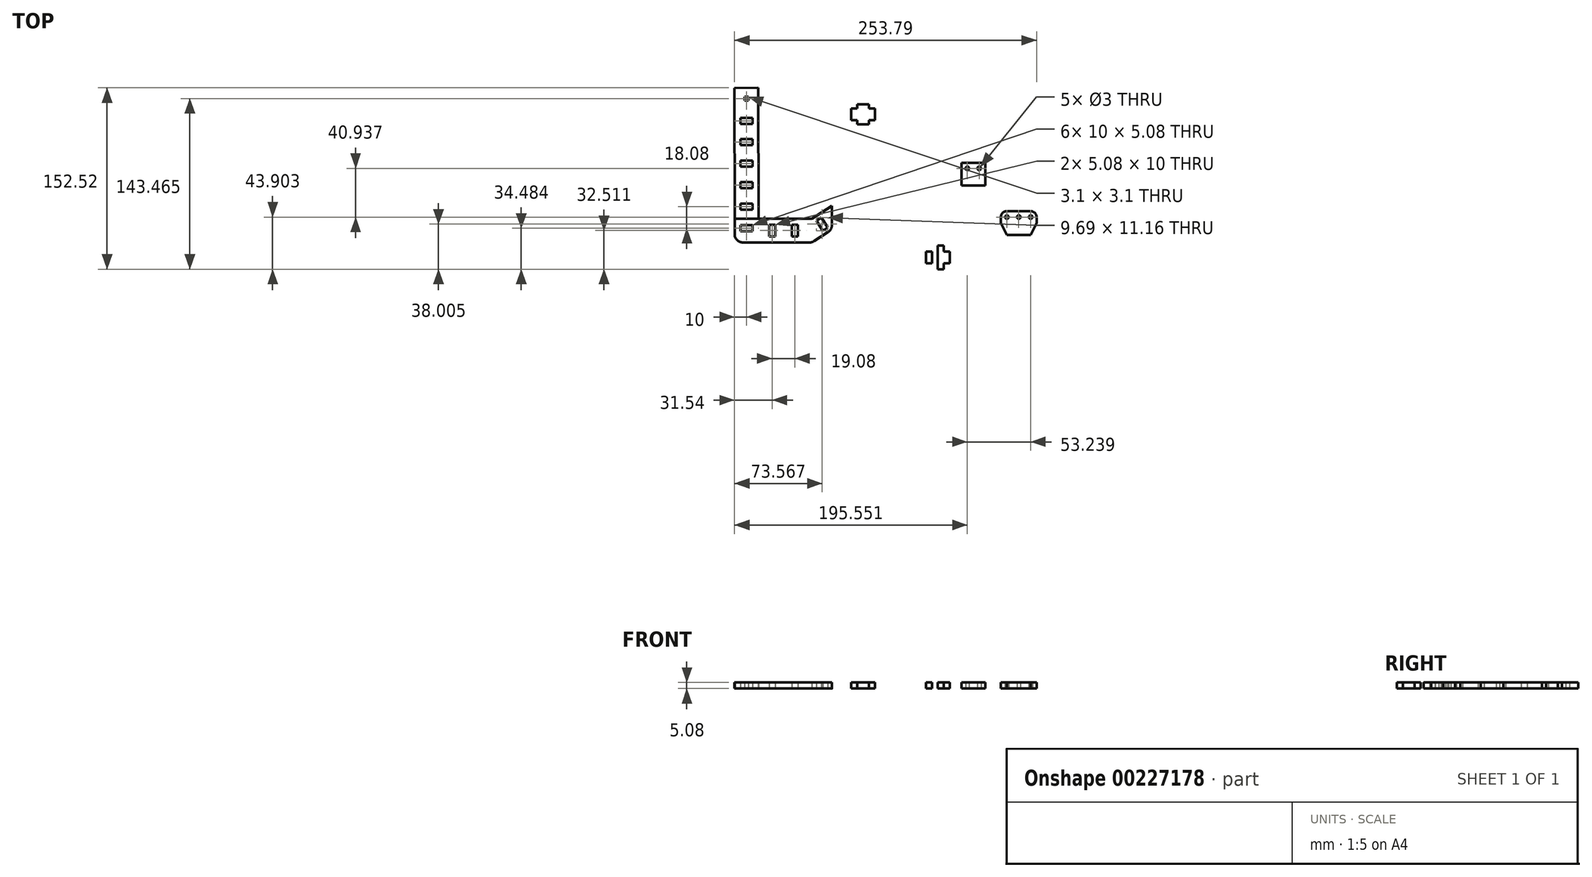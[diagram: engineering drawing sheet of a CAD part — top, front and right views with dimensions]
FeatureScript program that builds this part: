
annotation { "Feature Type Name" : "Feature", "Feature Type Description" : "" }
export const myFeature = defineFeature(function(context is Context, id is Id, definition is map)
    precondition{}
    {
        {
            var Q0;
            Q0=qCreatedBy(makeId("Top.planeOp"),FACE);
            var sketch = newSketch(context, id + "F0", { "sketchPlane" : qUnion([Q0])});
            skLineSegment(sketch, "E0.bottom", {"start": v(-72.75, 135.47) * mm, "end": v(-52.75, 135.48) * mm});
            skLineSegment(sketch, "E0.left", {"start": v(-72.75, 135.47) * mm, "end": v(-72.71, 25.47) * mm});
            skLineSegment(sketch, "E1.bottom", {"start": v(-57.75, 92.3) * mm, "end": v(-67.75, 92.3) * mm});
            skLineSegment(sketch, "E1.top", {"start": v(-57.75, 87.22) * mm, "end": v(-67.75, 87.22) * mm});
            skLineSegment(sketch, "E1.left", {"start": v(-57.75, 92.3) * mm, "end": v(-57.75, 87.22) * mm});
            skLineSegment(sketch, "E1.right", {"start": v(-67.75, 92.3) * mm, "end": v(-67.75, 87.22) * mm});
            skPoint(sketch, "E1.middle", {"position": v(-62.75, 89.76) * mm});
            skPoint(sketch, "E1.middle.positionSnap0", {"position": v(-62.75, 135.47) * mm});
            skLineSegment(sketch, "E2", {"start": v(-52.75, 135.48) * mm, "end": v(-52.71, 25.48) * mm});
            skLineSegment(sketch, "E3.bottom", {"start": v(-67.75, 74.22) * mm, "end": v(-57.75, 74.22) * mm});
            skLineSegment(sketch, "E3.top", {"start": v(-67.75, 69.14) * mm, "end": v(-57.75, 69.14) * mm});
            skLineSegment(sketch, "E3.left", {"start": v(-67.75, 74.22) * mm, "end": v(-67.75, 69.14) * mm});
            skLineSegment(sketch, "E3.right", {"start": v(-57.75, 74.22) * mm, "end": v(-57.75, 69.14) * mm});
            skLineSegment(sketch, "E4.bottom", {"start": v(117.8, 72.3) * mm, "end": v(137.8, 72.3) * mm});
            skLineSegment(sketch, "E4.top", {"start": v(117.8, 63.3) * mm, "end": v(137.8, 63.3) * mm});
            skLineSegment(sketch, "E4.left", {"start": v(117.8, 72.3) * mm, "end": v(117.8, 63.3) * mm});
            skLineSegment(sketch, "E4.right", {"start": v(137.8, 72.3) * mm, "end": v(137.8, 63.3) * mm});
            skCircle(sketch, "E5", {"center": v(122.8, 67.8) * mm, "radius": 1.5 * mm});
            skPoint(sketch, "E5.centerSnap0", {"position": v(117.8, 67.8) * mm});
            skLineSegment(sketch, "E6", {"start": v(127.8, 63.3) * mm, "end": v(127.8, 72.3) * mm, "construction": true});
            skCircle(sketch, "E7.MirrorC", {"center": v(132.8, 67.8) * mm, "radius": 1.5 * mm});
            skLineSegment(sketch, "E8.top", {"start": v(117.8, 53.3) * mm, "end": v(137.8, 53.3) * mm});
            skLineSegment(sketch, "E8.left", {"start": v(117.8, 63.3) * mm, "end": v(117.8, 53.3) * mm});
            skLineSegment(sketch, "E8.right", {"start": v(137.8, 63.3) * mm, "end": v(137.8, 53.3) * mm});
            skLineSegment(sketch, "E9.bottom", {"start": v(-57.75, 110.38) * mm, "end": v(-67.75, 110.38) * mm});
            skLineSegment(sketch, "E9.top", {"start": v(-57.75, 105.3) * mm, "end": v(-67.75, 105.3) * mm});
            skLineSegment(sketch, "E9.left", {"start": v(-57.75, 110.38) * mm, "end": v(-57.75, 105.3) * mm});
            skLineSegment(sketch, "E9.right", {"start": v(-67.75, 110.38) * mm, "end": v(-67.75, 105.3) * mm});
            skLineSegment(sketch, "E10", {"start": v(-67.75, 71.68) * mm, "end": v(-57.75, 71.68) * mm});
            skLineSegment(sketch, "E11.MirrorCS", {"start": v(-67.75, 51.06) * mm, "end": v(-67.75, 56.14) * mm});
            skLineSegment(sketch, "E12.MirrorCS", {"start": v(-57.75, 56.14) * mm, "end": v(-67.75, 56.14) * mm});
            skLineSegment(sketch, "E13.MirrorCS", {"start": v(-57.75, 51.06) * mm, "end": v(-57.75, 56.14) * mm});
            skLineSegment(sketch, "E14.MirrorCS", {"start": v(-57.75, 51.06) * mm, "end": v(-67.75, 51.06) * mm});
            skLineSegment(sketch, "E15", {"start": v(-67.75, 53.6) * mm, "end": v(-57.75, 53.6) * mm});
            skLineSegment(sketch, "E16.bottom", {"start": v(93.14, 2.96) * mm, "end": v(102.98, 2.96) * mm});
            skLineSegment(sketch, "E16.top", {"start": v(93.14, -17.04) * mm, "end": v(102.98, -17.04) * mm});
            skLineSegment(sketch, "E16.left", {"start": v(93.14, 2.96) * mm, "end": v(93.14, -17.04) * mm});
            skLineSegment(sketch, "E16.right", {"start": v(102.98, 2.96) * mm, "end": v(102.98, -17.04) * mm});
            skLineSegment(sketch, "E17.bottom", {"start": v(93.14, -2.04) * mm, "end": v(88.06, -2.04) * mm});
            skLineSegment(sketch, "E17.top", {"start": v(93.14, -12.04) * mm, "end": v(88.06, -12.04) * mm});
            skLineSegment(sketch, "E17.left", {"start": v(93.14, -2.04) * mm, "end": v(93.14, -12.04) * mm});
            skLineSegment(sketch, "E17.right", {"start": v(88.06, -2.04) * mm, "end": v(88.06, -12.04) * mm});
            skLineSegment(sketch, "E18", {"start": v(98.06, 2.96) * mm, "end": v(98.06, -17.04) * mm});
            skLineSegment(sketch, "E19.MirrorCS", {"start": v(102.98, -2.04) * mm, "end": v(108.06, -2.04) * mm});
            skLineSegment(sketch, "E20.MirrorCS", {"start": v(108.06, -2.04) * mm, "end": v(108.06, -12.04) * mm});
            skLineSegment(sketch, "E21.MirrorCS", {"start": v(102.98, -12.04) * mm, "end": v(108.06, -12.04) * mm});
            skLineSegment(sketch, "E22", {"start": v(-72.71, 25.47) * mm, "end": v(-52.71, 25.48) * mm});
            skLineSegment(sketch, "E23.bottom", {"start": v(-72.71, 25.47) * mm, "end": v(-7.71, 25.47) * mm});
            skLineSegment(sketch, "E23.top", {"start": v(-72.71, 5.47) * mm, "end": v(-7.71, 5.47) * mm});
            skLineSegment(sketch, "E23.left", {"start": v(-72.71, 25.47) * mm, "end": v(-72.71, 5.47) * mm});
            skLineSegment(sketch, "E23.right", {"start": v(-7.71, 25.47) * mm, "end": v(-7.71, 5.47) * mm});
            skLineSegment(sketch, "E24.MirrorCS", {"start": v(-67.75, 38.06) * mm, "end": v(-57.75, 38.06) * mm});
            skLineSegment(sketch, "E25.MirrorCS", {"start": v(-67.75, 32.98) * mm, "end": v(-67.75, 38.06) * mm});
            skLineSegment(sketch, "E26.MirrorCS", {"start": v(-57.75, 32.98) * mm, "end": v(-57.75, 38.06) * mm});
            skLineSegment(sketch, "E27.MirrorCS", {"start": v(-67.75, 32.98) * mm, "end": v(-57.75, 32.98) * mm});
            skPoint(sketch, "E28.middle", {"position": v(-35.82, 35.52) * mm});
            skPoint(sketch, "E28.middle.positionSnap0", {"position": v(-57.75, 35.52) * mm});
            skPoint(sketch, "E28.centerSnap0", {"position": v(-57.75, 35.52) * mm});
            skPoint(sketch, "E29.middle.positionSnap0", {"position": v(-33.28, 35.52) * mm});
            skPoint(sketch, "E29.centerSnap0", {"position": v(-33.28, 35.52) * mm});
            skPoint(sketch, "E30.middle", {"position": v(-3.93, 60.9) * mm});
            skPoint(sketch, "E30.middle.positionSnap0", {"position": v(-3.93, 68.63) * mm});
            skPoint(sketch, "E30.centerSnap0", {"position": v(-3.93, 68.63) * mm});
            skLineSegment(sketch, "E31", {"start": v(-7.71, 25.47) * mm, "end": v(9.1, 36.3) * mm});
            skLineSegment(sketch, "E32", {"start": v(-7.71, 5.47) * mm, "end": v(9.1, 16.3) * mm});
            skLineSegment(sketch, "E33", {"start": v(9.1, 16.3) * mm, "end": v(9.1, 36.3) * mm});
            skLineSegment(sketch, "E34", {"start": v(-4.03, 23.8) * mm, "end": v(0.25, 26.54) * mm});
            skLineSegment(sketch, "E35", {"start": v(0.25, 26.54) * mm, "end": v(5.66, 18.14) * mm});
            skLineSegment(sketch, "E36", {"start": v(5.66, 18.14) * mm, "end": v(1.39, 15.39) * mm});
            skLineSegment(sketch, "E37", {"start": v(1.39, 15.39) * mm, "end": v(-4.03, 23.8) * mm});
            skLineSegment(sketch, "E38.bottom", {"start": v(40.24, 121.66) * mm, "end": v(30.4, 121.66) * mm});
            skLineSegment(sketch, "E38.top", {"start": v(40.24, 104.84) * mm, "end": v(30.4, 104.84) * mm});
            skLineSegment(sketch, "E38.left", {"start": v(40.24, 121.66) * mm, "end": v(40.24, 104.84) * mm});
            skLineSegment(sketch, "E38.right", {"start": v(30.4, 121.66) * mm, "end": v(30.4, 104.84) * mm});
            skPoint(sketch, "E38.middle", {"position": v(35.32, 113.25) * mm});
            skLineSegment(sketch, "E39.bottom", {"start": v(40.24, 118.25) * mm, "end": v(45.32, 118.25) * mm});
            skLineSegment(sketch, "E39.top", {"start": v(40.24, 108.25) * mm, "end": v(45.32, 108.25) * mm});
            skLineSegment(sketch, "E39.left", {"start": v(40.24, 118.25) * mm, "end": v(40.24, 108.25) * mm});
            skLineSegment(sketch, "E39.right", {"start": v(45.32, 118.25) * mm, "end": v(45.32, 108.25) * mm});
            skLineSegment(sketch, "E40", {"start": v(35.32, 121.66) * mm, "end": v(35.32, 104.84) * mm, "construction": true});
            skLineSegment(sketch, "E41.MirrorCS", {"start": v(30.4, 118.25) * mm, "end": v(25.32, 118.25) * mm});
            skLineSegment(sketch, "E42.MirrorCS", {"start": v(25.32, 118.25) * mm, "end": v(25.32, 108.25) * mm});
            skLineSegment(sketch, "E43.MirrorCS", {"start": v(30.4, 108.25) * mm, "end": v(25.32, 108.25) * mm});
            skLineSegment(sketch, "E44.MirrorCS", {"start": v(-67.75, 14.9) * mm, "end": v(-67.75, 19.98) * mm});
            skLineSegment(sketch, "E45.MirrorCS", {"start": v(-57.75, 14.9) * mm, "end": v(-67.75, 14.9) * mm});
            skLineSegment(sketch, "E46.MirrorCS", {"start": v(-57.75, 19.98) * mm, "end": v(-67.75, 19.98) * mm});
            skLineSegment(sketch, "E47.MirrorCS", {"start": v(-57.75, 14.9) * mm, "end": v(-57.75, 19.98) * mm});
            skLineSegment(sketch, "E48.bottom", {"start": v(-38.67, 20.47) * mm, "end": v(-43.75, 20.47) * mm});
            skLineSegment(sketch, "E48.top", {"start": v(-38.67, 10.47) * mm, "end": v(-43.75, 10.47) * mm});
            skLineSegment(sketch, "E48.left", {"start": v(-38.67, 20.47) * mm, "end": v(-38.67, 10.47) * mm});
            skLineSegment(sketch, "E48.right", {"start": v(-43.75, 20.47) * mm, "end": v(-43.75, 10.47) * mm});
            skPoint(sketch, "E48.middle", {"position": v(-41.21, 15.47) * mm});
            skPoint(sketch, "E48.middle.positionSnap0", {"position": v(-57.75, 17.44) * mm});
            skLineSegment(sketch, "E49.bottom", {"start": v(179.2, 50.76) * mm, "end": v(149.19, 50.76) * mm});
            skLineSegment(sketch, "E49.top", {"start": v(179.2, 37.82) * mm, "end": v(149.19, 37.82) * mm});
            skLineSegment(sketch, "E49.left", {"start": v(179.2, 50.76) * mm, "end": v(179.2, 37.82) * mm});
            skLineSegment(sketch, "E49.right", {"start": v(149.19, 50.76) * mm, "end": v(149.19, 37.82) * mm});
            skPoint(sketch, "E49.middle", {"position": v(164.2, 44.29) * mm});
            skCircle(sketch, "E50", {"center": v(156.04, 26.86) * mm, "radius": 1.5 * mm});
            skLineSegment(sketch, "E51", {"start": v(156.04, 26.86) * mm, "end": v(176.04, 26.86) * mm});
            skCircle(sketch, "E52", {"center": v(176.04, 26.86) * mm, "radius": 1.5 * mm});
            skCircle(sketch, "E53", {"center": v(166.04, 26.86) * mm, "radius": 1.5 * mm});
            skLineSegment(sketch, "E54.bottom", {"start": v(181.04, 31.86) * mm, "end": v(151.04, 31.86) * mm});
            skLineSegment(sketch, "E54.top", {"start": v(181.04, 21.86) * mm, "end": v(151.04, 21.86) * mm});
            skLineSegment(sketch, "E54.left", {"start": v(181.04, 31.86) * mm, "end": v(181.04, 21.86) * mm});
            skLineSegment(sketch, "E54.right", {"start": v(151.04, 31.86) * mm, "end": v(151.04, 21.86) * mm});
            skLineSegment(sketch, "E55.bottom", {"start": v(176.04, 21.86) * mm, "end": v(156.04, 21.86) * mm});
            skLineSegment(sketch, "E55.top", {"start": v(176.04, 11.86) * mm, "end": v(156.04, 11.86) * mm});
            skLineSegment(sketch, "E55.left", {"start": v(176.04, 21.86) * mm, "end": v(176.04, 11.86) * mm});
            skLineSegment(sketch, "E55.right", {"start": v(156.04, 21.86) * mm, "end": v(156.04, 11.86) * mm});
            skPoint(sketch, "E55.middle", {"position": v(166.04, 16.86) * mm});
            skPoint(sketch, "E55.middle.positionSnap0", {"position": v(166.04, 21.86) * mm});
            skPoint(sketch, "E55.centerSnap0", {"position": v(166.04, 21.86) * mm});
            skLineSegment(sketch, "E56", {"start": v(166.04, 21.86) * mm, "end": v(166.04, 11.86) * mm, "construction": true});
            skLineSegment(sketch, "E57.bottom", {"start": v(-24.67, 20.47) * mm, "end": v(-19.6, 20.47) * mm});
            skLineSegment(sketch, "E57.top", {"start": v(-24.67, 10.47) * mm, "end": v(-19.6, 10.47) * mm});
            skLineSegment(sketch, "E57.left", {"start": v(-24.67, 20.47) * mm, "end": v(-24.67, 10.47) * mm});
            skLineSegment(sketch, "E57.right", {"start": v(-19.6, 20.47) * mm, "end": v(-19.6, 10.47) * mm});
            skPoint(sketch, "E57.middle", {"position": v(-22.13, 15.47) * mm});
            skLineSegment(sketch, "E58", {"start": v(151.04, 21.86) * mm, "end": v(156.04, 11.86) * mm});
            skLineSegment(sketch, "E59.MirrorCS", {"start": v(181.04, 21.86) * mm, "end": v(176.04, 11.86) * mm});
            skLineSegment(sketch, "E60.bottom", {"start": v(-61.2, 127.97) * mm, "end": v(-64.3, 127.97) * mm});
            skLineSegment(sketch, "E60.top", {"start": v(-61.2, 124.87) * mm, "end": v(-64.3, 124.87) * mm});
            skLineSegment(sketch, "E60.left", {"start": v(-61.2, 127.97) * mm, "end": v(-61.2, 124.87) * mm});
            skLineSegment(sketch, "E60.right", {"start": v(-64.3, 127.97) * mm, "end": v(-64.3, 124.87) * mm});
            skPoint(sketch, "E60.middle", {"position": v(-62.75, 126.42) * mm});
            skSolve(sketch);
        }
        {
            var Q0;
            Q0=makeQuery(id+"F0.imprint","IMPRINT",FACE,{"disambiguationData":[TD([[makeQuery(id+"F0.imprint","IMPRINT",EDGE,{"derivedFrom":sQuery(id+"F0.wireOp",EDGE,"E0.top")}),-1.0]])]});
            var Q1;
            Q1=makeQuery(id+"F0.imprint","IMPRINT",FACE,{"disambiguationData":[TD([[makeQuery(id+"F0.imprint","IMPRINT",EDGE,{"derivedFrom":sQuery(id+"F0.wireOp",EDGE,"E0.bottom")}),-1.0]])]});
            var Q2;
            Q2=makeQuery(id+"F0.imprint","IMPRINT",FACE,{"disambiguationData":[TD([[makeQuery(id+"F0.imprint","IMPRINT",EDGE,{"derivedFrom":sQuery(id+"F0.wireOp",EDGE,"MHB96mG5-6ORf-qB09-eiFa-LkEqSb64jFLL.right")}),1.0]])]});
            var Q3;
            {var subQ1=sQuery(id+"F0.wireOp",EDGE,"E4.right");Q3=makeQuery(id+"F0.imprint","IMPRINT",FACE,{"disambiguationData":[TD([[makeQuery(id+"F0.imprint","IMPRINT",EDGE,{"derivedFrom":subQ1}),-1.0]])]});}
            var Q4;
            {var subQ0=sQuery(id+"F0.wireOp",EDGE,"E4.left");Q4=makeQuery(id+"F0.imprint","IMPRINT",FACE,{"disambiguationData":[TD([[makeQuery(id+"F0.imprint","IMPRINT",EDGE,{"derivedFrom":subQ0}),1.0]])]});}
            var Q5;
            {var subQ3=sQuery(id+"F0.wireOp",EDGE,"E4.left");Q5=makeQuery(id+"F0.imprint","IMPRINT",FACE,{"disambiguationData":[TD([[makeQuery(id+"F0.imprint","IMPRINT",EDGE,{"derivedFrom":subQ3}),-1.0]])]});}
            var Q6;
            {var subQ1=sQuery(id+"F0.wireOp",EDGE,"E4.right");Q6=makeQuery(id+"F0.imprint","IMPRINT",FACE,{"disambiguationData":[TD([[makeQuery(id+"F0.imprint","IMPRINT",EDGE,{"derivedFrom":subQ1}),1.0]])]});}
            var Q7;
            Q7=makeQuery(id+"F0.imprint","IMPRINT",FACE,{"disambiguationData":[TD([[makeQuery(id+"F0.imprint","IMPRINT",EDGE,{"derivedFrom":sQuery(id+"F0.wireOp",EDGE,"FHUylIf5-C3kQ-FjqG-YRcO-ydNnjkUGeUD1.top")}),-1.0]])]});
            var Q8;
            {var subQ0=sQuery(id+"F0.wireOp",EDGE,"7eModG5b-Kflo-Nrth-XOn8-6tDt67gPotOb");Q8=makeQuery(id+"F0.imprint","IMPRINT",FACE,{"disambiguationData":[TD([[makeQuery(id+"F0.imprint","IMPRINT",EDGE,{"derivedFrom":subQ0}),1.0]])]});}
            var Q9;
            {var subQ2=sQuery(id+"F0.wireOp",EDGE,"42d3f06b-e886-45a1-b02d-900de482a10a0.MirrorCS");Q9=makeQuery(id+"F0.imprint","IMPRINT",FACE,{"disambiguationData":[TD([[makeQuery(id+"F0.imprint","IMPRINT",EDGE,{"derivedFrom":subQ2}),1.0]])]});}
            var Q10;
            Q10=makeQuery(id+"F0.imprint","IMPRINT",FACE,{"disambiguationData":[TD([[makeQuery(id+"F0.imprint","IMPRINT",EDGE,{"derivedFrom":sQuery(id+"F0.wireOp",EDGE,"E8.top")}),1.0]])]});
            var Q11;
            {var subQ3=sQuery(id+"F0.wireOp",EDGE,"3tS85iKH-YX9D-ETo1-o1gY-4SngDrgIYCuw");Q11=makeQuery(id+"F0.imprint","IMPRINT",FACE,{"disambiguationData":[TD([[makeQuery(id+"F0.imprint","IMPRINT",EDGE,{"derivedFrom":subQ3}),-1.0]])]});}
            var Q12;
            {var subQ0=sQuery(id+"F0.wireOp",EDGE,"MHB96mG5-6ORf-qB09-eiFa-LkEqSb64jFLL.right");Q12=makeQuery(id+"F0.imprint","IMPRINT",FACE,{"disambiguationData":[TD([[makeQuery(id+"F0.imprint","IMPRINT",EDGE,{"derivedFrom":subQ0}),-1.0]])]});}
            var Q13;
            Q13=makeQuery(id+"F0.imprint","IMPRINT",FACE,{"disambiguationData":[TD([[makeQuery(id+"F0.imprint","IMPRINT",EDGE,{"derivedFrom":sQuery(id+"F0.wireOp",EDGE,"E17.bottom")}),1.0]])]});
            var Q14;
            {var subQ5=sQuery(id+"F0.wireOp",EDGE,"E18");Q14=makeQuery(id+"F0.imprint","IMPRINT",FACE,{"disambiguationData":[TD([[makeQuery(id+"F0.imprint","IMPRINT",EDGE,{"derivedFrom":subQ5}),1.0]])]});}
            var Q15;
            {var subQ3=sQuery(id+"F0.wireOp",EDGE,"E17.left");Q15=makeQuery(id+"F0.imprint","IMPRINT",FACE,{"disambiguationData":[TD([[makeQuery(id+"F0.imprint","IMPRINT",EDGE,{"derivedFrom":subQ3}),1.0]])]});}
            var Q16;
            {var subQ0=sQuery(id+"F0.wireOp",EDGE,"E19.MirrorCS");Q16=makeQuery(id+"F0.imprint","IMPRINT",FACE,{"disambiguationData":[TD([[makeQuery(id+"F0.imprint","IMPRINT",EDGE,{"derivedFrom":subQ0}),-1.0]])]});}
            var Q17;
            {var subQ5=sQuery(id+"F0.wireOp",EDGE,"fGFLzmHS-5t6t-uwHw-qYU0-MsMaWPDrigGM");Q17=makeQuery(id+"F0.imprint","IMPRINT",FACE,{"disambiguationData":[TD([[makeQuery(id+"F0.imprint","IMPRINT",EDGE,{"derivedFrom":subQ5}),-1.0]])]});}
            var Q18;
            {var subQ0=sQuery(id+"F0.wireOp",EDGE,"b1567171-7321-411e-b19b-313b392d97f40.MirrorCS");Q18=makeQuery(id+"F0.imprint","IMPRINT",FACE,{"disambiguationData":[TD([[makeQuery(id+"F0.imprint","IMPRINT",EDGE,{"derivedFrom":subQ0}),1.0]])]});}
            var Q19;
            Q19=makeQuery(id+"F0.imprint","IMPRINT",FACE,{"disambiguationData":[TD([[makeQuery(id+"F0.imprint","IMPRINT",EDGE,{"derivedFrom":sQuery(id+"F0.wireOp",EDGE,"zO6hTq61-RiQV-N2gz-YrrV-uKpAPromDpzJ")}),1.0]])]});
            var Q20;
            Q20=makeQuery(id+"F0.imprint","IMPRINT",FACE,{"disambiguationData":[TD([[makeQuery(id+"F0.imprint","IMPRINT",EDGE,{"derivedFrom":sQuery(id+"F0.wireOp",EDGE,"la3SCKXS-RNir-esm8-qc2e-MOpLKnUuBaJe")}),-1.0]])]});
            var Q21;
            Q21=makeQuery(id+"F0.imprint","IMPRINT",FACE,{"disambiguationData":[TD([[makeQuery(id+"F0.imprint","IMPRINT",EDGE,{"derivedFrom":sQuery(id+"F0.wireOp",EDGE,"c3KznoZc-OUrc-sfPT-s7lm-P0rAdTupKzcw")}),-1.0]])]});
            var Q22;
            Q22=makeQuery(id+"F0.imprint","IMPRINT",FACE,{"disambiguationData":[TD([[makeQuery(id+"F0.imprint","IMPRINT",EDGE,{"derivedFrom":sQuery(id+"F0.wireOp",EDGE,"Dby1ULce-0gBK-EZdE-0ygd-gGV5t3pFWjds")}),-1.0]])]});
            var Q23;
            {var subQ0=sQuery(id+"F0.wireOp",EDGE,"8MNtdiwC-oDEb-32Q9-EgMT-ZNvNkAF6i7Vc");Q23=makeQuery(id+"F0.imprint","IMPRINT",FACE,{"disambiguationData":[TD([[makeQuery(id+"F0.imprint","IMPRINT",EDGE,{"derivedFrom":subQ0}),1.0]])]});}
            var Q24;
            Q24=makeQuery(id+"F0.imprint","IMPRINT",FACE,{"disambiguationData":[TD([[makeQuery(id+"F0.imprint","IMPRINT",EDGE,{"derivedFrom":sQuery(id+"F0.wireOp",EDGE,"E23.top")}),1.0]])]});
            var Q25;
            {var subQ3=sQuery(id+"F0.wireOp",EDGE,"FJ9boMJA-qFNb-msr4-57uS-0Kpx15RZBF1s.bottom");Q25=makeQuery(id+"F0.imprint","IMPRINT",FACE,{"disambiguationData":[TD([[makeQuery(id+"F0.imprint","IMPRINT",EDGE,{"derivedFrom":subQ3}),1.0]])]});}
            var Q26;
            Q26=makeQuery(id+"F0.imprint","IMPRINT",FACE,{"disambiguationData":[TD([[makeQuery(id+"F0.imprint","IMPRINT",EDGE,{"derivedFrom":sQuery(id+"F0.wireOp",EDGE,"E23.right")}),1.0]])]});
            var Q27;
            {var subQ3=sQuery(id+"F0.wireOp",EDGE,"E38.bottom");Q27=makeQuery(id+"F0.imprint","IMPRINT",FACE,{"disambiguationData":[TD([[makeQuery(id+"F0.imprint","IMPRINT",EDGE,{"derivedFrom":subQ3}),1.0]])]});}
            var Q28;
            Q28=makeQuery(id+"F0.imprint","IMPRINT",FACE,{"disambiguationData":[TD([[makeQuery(id+"F0.imprint","IMPRINT",EDGE,{"derivedFrom":sQuery(id+"F0.wireOp",EDGE,"E39.bottom")}),-1.0]])]});
            var Q29;
            {var subQ0=sQuery(id+"F0.wireOp",EDGE,"E41.MirrorCS");Q29=makeQuery(id+"F0.imprint","IMPRINT",FACE,{"disambiguationData":[TD([[makeQuery(id+"F0.imprint","IMPRINT",EDGE,{"derivedFrom":subQ0}),1.0]])]});}
            var Q30;
            Q30=makeQuery(id+"F0.imprint","IMPRINT",FACE,{"disambiguationData":[TD([[makeQuery(id+"F0.imprint","IMPRINT",EDGE,{"derivedFrom":sQuery(id+"F0.wireOp",EDGE,"E50")}),-1.0]])]});
            var Q31;
            {var subQ0=sQuery(id+"F0.wireOp",EDGE,"FZNawtLh-T8mD-ZIeX-cusq-QjliIw30ABOg");Q31=makeQuery(id+"F0.imprint","IMPRINT",FACE,{"disambiguationData":[TD([[makeQuery(id+"F0.imprint","IMPRINT",EDGE,{"derivedFrom":subQ0}),-1.0]])]});}
            var Q32;
            Q32=makeQuery(id+"F0.imprint","IMPRINT",FACE,{"disambiguationData":[TD([[makeQuery(id+"F0.imprint","IMPRINT",EDGE,{"derivedFrom":sQuery(id+"F0.wireOp",EDGE,"E55.right")}),-1.0]])]});
            var Q33;
            Q33=makeQuery(id+"F0.imprint","IMPRINT",FACE,{"disambiguationData":[TD([[makeQuery(id+"F0.imprint","IMPRINT",EDGE,{"derivedFrom":sQuery(id+"F0.wireOp",EDGE,"E55.top")}),-1.0]])]});
            var Q34;
            {var subQ0=sQuery(id+"F0.wireOp",EDGE,"a1829607-81be-4423-be01-0f0e7b78aaa70.MirrorCS");Q34=makeQuery(id+"F0.imprint","IMPRINT",FACE,{"disambiguationData":[TD([[makeQuery(id+"F0.imprint","IMPRINT",EDGE,{"derivedFrom":subQ0}),1.0]])]});}
            var Q35;
            Q35=makeQuery(id+"F0.imprint","IMPRINT",FACE,{"disambiguationData":[TD([[makeQuery(id+"F0.imprint","IMPRINT",EDGE,{"derivedFrom":sQuery(id+"F0.wireOp",EDGE,"E55.left")}),1.0]])]});
            extrude(context, id + "F1", {"entities" : qUnion([Q0, Q1, Q2, Q3, Q4, Q5, Q6, Q7, Q8, Q9, Q10, Q11, Q12, Q13, Q14, Q15, Q16, Q17, Q18, Q19, Q20, Q21, Q22, Q23, Q24, Q25, Q26, Q27, Q28, Q29, Q30, Q31, Q32, Q33, Q34, Q35]), "depth" : 5.08 * mm, "offsetDistance" : 25 * mm});
        }
        {
            var Q0;
            Q0=makeQuery(id+"F1.opExtrude","SWEPT_EDGE",EDGE,{"disambiguationData":[OSD([sQuery(id+"F0.wireOp",EDGE,"E23.top"),sQuery(id+"F0.wireOp",EDGE,"E23.left")])]});
            var Q1;
            Q1=makeQuery(id+"F1.opExtrude","SWEPT_EDGE",EDGE,{"disambiguationData":[OSD([sQuery(id+"F0.wireOp",EDGE,"E23.top"),sQuery(id+"F0.wireOp",EDGE,"E23.right"),sQuery(id+"F0.wireOp",EDGE,"E32")])]});
            var Q2;
            Q2=makeQuery(id+"F1.opExtrude","SWEPT_EDGE",EDGE,{"disambiguationData":[OSD([sQuery(id+"F0.wireOp",EDGE,"E32"),sQuery(id+"F0.wireOp",EDGE,"E33")])]});
            fillet(context, id + "F2", {"entities" : qUnion([Q0, Q1, Q2]), "radius" : 7 * mm, "tangentPropagation" : true, "allowEdgeOverflow" : false});
        }
        {
            var Q0;
            Q0=makeQuery(id+"F1.opExtrude","SWEPT_EDGE",EDGE,{"disambiguationData":[OSD([sQuery(id+"F0.wireOp",EDGE,"E54.bottom"),sQuery(id+"F0.wireOp",EDGE,"E54.right")])]});
            var Q1;
            Q1=makeQuery(id+"F1.opExtrude","SWEPT_EDGE",EDGE,{"disambiguationData":[OSD([sQuery(id+"F0.wireOp",EDGE,"E54.bottom"),sQuery(id+"F0.wireOp",EDGE,"E54.left")])]});
            fillet(context, id + "F3", {"entities" : qUnion([Q0, Q1]), "radius" : 5 * mm, "tangentPropagation" : true, "allowEdgeOverflow" : false});
        }
    });
